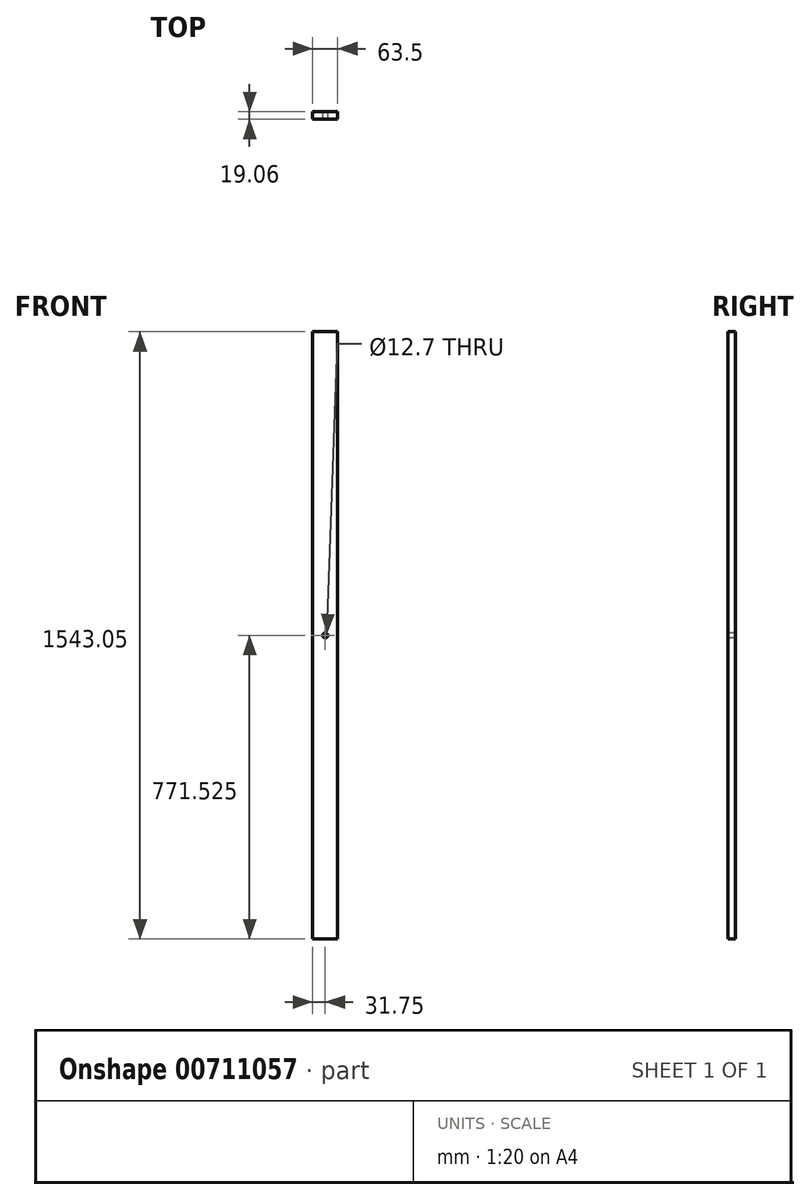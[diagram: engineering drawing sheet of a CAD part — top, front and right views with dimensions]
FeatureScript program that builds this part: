
annotation { "Feature Type Name" : "Feature", "Feature Type Description" : "" }
export const myFeature = defineFeature(function(context is Context, id is Id, definition is map)
    precondition{}
    {
        {
            var Q0;
            Q0=qCreatedBy(makeId("Top.planeOp"),FACE);
            var sketch = newSketch(context, id + "F0", { "sketchPlane" : qUnion([Q0])});
            skLineSegment(sketch, "E0.bottom", {"start": v(31.75, 9.53) * mm, "end": v(-31.75, 9.53) * mm});
            skLineSegment(sketch, "E0.top", {"start": v(31.75, -9.53) * mm, "end": v(-31.75, -9.53) * mm});
            skLineSegment(sketch, "E0.left", {"start": v(31.75, 9.53) * mm, "end": v(31.75, -9.52) * mm});
            skLineSegment(sketch, "E0.right", {"start": v(-31.75, 9.53) * mm, "end": v(-31.75, -9.52) * mm});
            skPoint(sketch, "E0.middle", {"position": v(0, 0) * mm});
            skSolve(sketch);
        }
        {
            var Q0;
            Q0=makeQuery(id+"F0.imprint","IMPRINT",FACE,{"disambiguationData":[TD([[makeQuery(id+"F0.imprint","IMPRINT",EDGE,{"derivedFrom":sQuery(id+"F0.wireOp",EDGE,"E0.bottom")}),1.0]])]});
            extrude(context, id + "F1", {"entities" : qUnion([Q0]), "depth" : 1543.05 * mm, "offsetDistance" : 25.4 * mm});
        }
        {
            var Q0;
            Q0=makeQuery(id+"F1.opExtrude","SWEPT_FACE",FACE,{"disambiguationData":[OSD([sQuery(id+"F0.wireOp",EDGE,"E0.top")])]});
            var sketch = newSketch(context, id + "F2", { "sketchPlane" : qUnion([Q0])});
            skLineSegment(sketch, "E1", {"start": v(-31.75, 771.53) * mm, "end": v(31.75, 771.53) * mm});
            skCircle(sketch, "E2", {"center": v(0, 771.53) * mm, "radius": 6.35 * mm});
            skSolve(sketch);
        }
        {
            var Q0;
            Q0 = qSketchRegion(id + "F2", true);
            extrude(context, id + "F3", {"entities" : qUnion([Q0]), "operationType" : NewBodyOperationType.REMOVE, "oppositeDirection" : true, "depth" : 25.4 * mm, "offsetDistance" : 25.4 * mm});
        }
    });
